# Revit family: Legrand_Gestion_eclairage_Detect_mvt_autonome_360D_Mur
name_source: partatom
category: Dispositifs d'éclairage
units: mm (PartAtom-declared; Revit-internal decimal feet)

## family parameters
Conserver l'orientation des annotations = Oui
Cote de connecteur circulaire = Utiliser le diamètre
Couper avec des vides une fois chargée = Non
Hôte = Face
Partagée = Non
Point de calcul de pièce = Non
Type d'élément = Normal

## types (1)
- Legrand_Gestion_eclairage_Detect_mvt_autonome_360D_Mur
    Adapté pour transmission sans fil = non
    Angle de détection horizontal (MAX) (°) = 360
    Angle de détection horizontal (MIN) (°) = 0
    Capacité de coupure max (W) = 1000
    Classe de protection (IP) = IP55
    Code d'assemblage = D5010200
    Condition Générale d'Utilisation = https://export.legrand.com
    Couleur = blanc
    Coupure forcée = non
    Courant de démarrage max (A) = 4.3
    Description = DETECT DE MOUVEMENT PIR 360 DEGRES MUR PLAFOND IP55
    Durée d'enclenchement max (mn) = 10
    Durée d'enclenchement min (s) = 10
    ETIM-5.0 Class = EC000133
    Elévation par défaut = 2500 mm  [stored 8.2021 ft]
    Entrée secondaire = non
    Exécution = détecteur de mouvement
    Fabricant = LEGRAND
    Fonction variateur intégrée = non
    Fréquence (MAX) (Hz) = 60
    Fréquence (MIN) (Hz) = 50
    Gestion CVC = non
    Gestion alarme = non
    Hauteur maxi de montage (m) = 2.5
    Image du type = PH6-Mural.jpg
    Mode de montage = apparent
    Numéro RAL = 9003
    Product ID = 048943
    Réglage de lumière constante = oui
    Sensibilité lumineuse (MAX) (lx) = 1275
    Sensibilité lumineuse (MIN) (lx) = 5
    Sensibilité lumineuse réglable = oui
    Sensibilité réglable = non
    Température (MAX) (°C) = 45
    Température (MIN) (°C) = -5
    Tension nominale (V) = 230
    Type de tension = AC
    Télécommandable = non
    URL = http://www.legrandoc.com

note: [stored X ft] marks values corroborated as IEEE doubles in the binary element streams (Revit-internal decimal feet)
